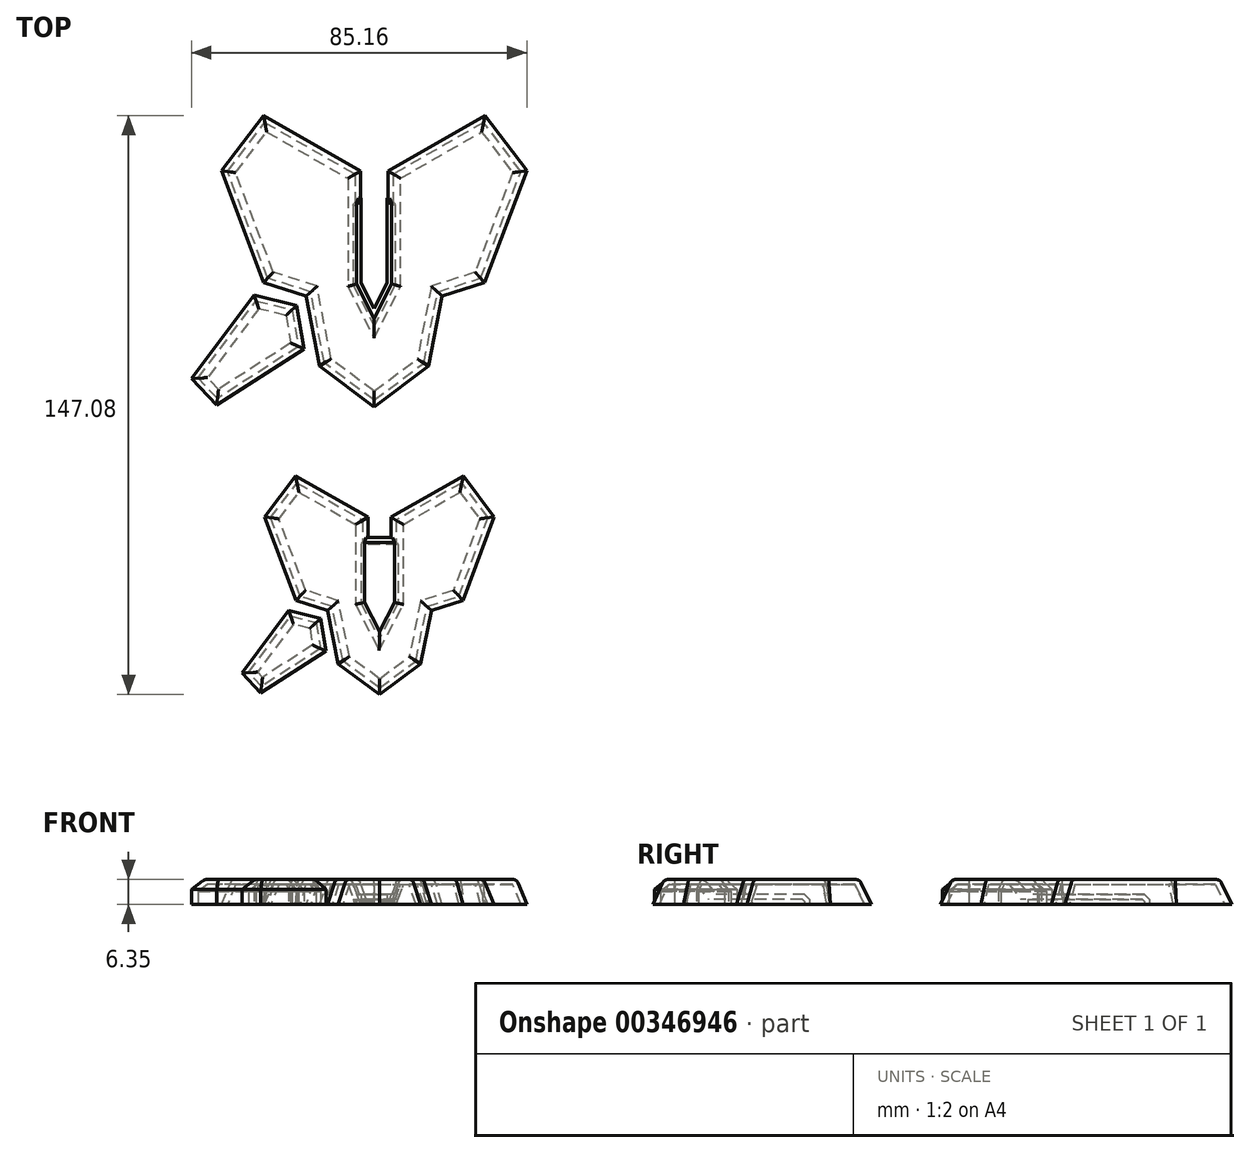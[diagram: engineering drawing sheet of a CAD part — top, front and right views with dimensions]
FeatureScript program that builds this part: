
annotation { "Feature Type Name" : "Feature", "Feature Type Description" : "" }
export const myFeature = defineFeature(function(context is Context, id is Id, definition is map)
    precondition{}
    {
        {
            var Q0;
            Q0=qCreatedBy(makeId("Top.planeOp"),FACE);
            var sketch = newSketch(context, id + "F0", { "sketchPlane" : qUnion([Q0])});
            skLineSegment(sketch, "E0", {"start": v(0.22, 21.79) * mm, "end": v(-3.27, 28.65) * mm});
            skLineSegment(sketch, "E1", {"start": v(-3.27, 28.65) * mm, "end": v(-3.27, 57.26) * mm});
            skLineSegment(sketch, "E2", {"start": v(-3.27, 57.26) * mm, "end": v(-28.23, 71.53) * mm});
            skLineSegment(sketch, "E3", {"start": v(-28.23, 71.53) * mm, "end": v(-39.05, 57.26) * mm});
            skLineSegment(sketch, "E4", {"start": v(-39.05, 57.26) * mm, "end": v(-28.26, 28.65) * mm});
            skLineSegment(sketch, "E5", {"start": v(-28.26, 28.65) * mm, "end": v(-17.5, 25.2) * mm});
            skLineSegment(sketch, "E6", {"start": v(-17.5, 25.2) * mm, "end": v(-14.07, 7.42) * mm});
            skLineSegment(sketch, "E7", {"start": v(-14.07, 7.42) * mm, "end": v(0.22, -3.25) * mm});
            skLineSegment(sketch, "E8", {"start": v(-30.55, 25.57) * mm, "end": v(-19.72, 22.92) * mm});
            skLineSegment(sketch, "E9", {"start": v(-19.72, 22.92) * mm, "end": v(-17.85, 11.94) * mm});
            skLineSegment(sketch, "E10", {"start": v(-17.85, 11.94) * mm, "end": v(-40.04, -2.32) * mm});
            skLineSegment(sketch, "E11", {"start": v(-40.04, -2.32) * mm, "end": v(-46.37, 4.42) * mm});
            skLineSegment(sketch, "E12", {"start": v(-46.37, 4.42) * mm, "end": v(-30.55, 25.57) * mm});
            skLineSegment(sketch, "E13", {"start": v(0.22, 18.03) * mm, "end": v(-6.84, 28.75) * mm});
            skLineSegment(sketch, "E14", {"start": v(-6.84, 28.75) * mm, "end": v(-6.84, 50.27) * mm});
            skLineSegment(sketch, "E15", {"start": v(-6.84, 50.27) * mm, "end": v(0.22, 50.27) * mm});
            skLineSegment(sketch, "E16.MirrorCS", {"start": v(6.84, 50.27) * mm, "end": v(-0.22, 50.27) * mm});
            skLineSegment(sketch, "E17.MirrorCS", {"start": v(6.84, 28.75) * mm, "end": v(6.84, 50.27) * mm});
            skLineSegment(sketch, "E18.MirrorCS", {"start": v(3.27, 28.65) * mm, "end": v(3.27, 57.26) * mm});
            skLineSegment(sketch, "E19.MirrorCS", {"start": v(-0.22, 21.79) * mm, "end": v(3.27, 28.65) * mm});
            skLineSegment(sketch, "E20.MirrorCS", {"start": v(-0.22, 18.03) * mm, "end": v(6.84, 28.75) * mm});
            skLineSegment(sketch, "E21.MirrorCS", {"start": v(3.27, 57.26) * mm, "end": v(28.23, 71.53) * mm});
            skLineSegment(sketch, "E22.MirrorCS", {"start": v(28.23, 71.53) * mm, "end": v(39.05, 57.26) * mm});
            skLineSegment(sketch, "E23.MirrorCS", {"start": v(39.05, 57.26) * mm, "end": v(28.26, 28.65) * mm});
            skLineSegment(sketch, "E24.MirrorCS", {"start": v(28.26, 28.65) * mm, "end": v(17.5, 25.2) * mm});
            skLineSegment(sketch, "E25.MirrorCS", {"start": v(17.5, 25.2) * mm, "end": v(14.07, 7.42) * mm});
            skLineSegment(sketch, "E26.MirrorCS", {"start": v(14.07, 7.42) * mm, "end": v(-0.22, -3.25) * mm});
            skLineSegment(sketch, "E27", {"start": v(1.32, -60) * mm, "end": v(-4.03, -52.16) * mm});
            skLineSegment(sketch, "E28", {"start": v(-4.03, -52.16) * mm, "end": v(-4.03, -36.02) * mm});
            skLineSegment(sketch, "E29", {"start": v(-4.03, -36.02) * mm, "end": v(1.32, -36.02) * mm});
            skLineSegment(sketch, "E30", {"start": v(1.32, -57.3) * mm, "end": v(-1.33, -52.15) * mm});
            skLineSegment(sketch, "E31", {"start": v(-1.33, -52.15) * mm, "end": v(-1.33, -30.7) * mm});
            skLineSegment(sketch, "E32", {"start": v(-1.33, -30.7) * mm, "end": v(-20.04, -20.02) * mm});
            skLineSegment(sketch, "E33", {"start": v(-20.04, -20.02) * mm, "end": v(-28.1, -30.7) * mm});
            skLineSegment(sketch, "E34", {"start": v(-28.1, -30.7) * mm, "end": v(-20.05, -52.16) * mm});
            skLineSegment(sketch, "E35", {"start": v(-20.05, -52.16) * mm, "end": v(-12.05, -54.72) * mm});
            skLineSegment(sketch, "E36", {"start": v(-12.05, -54.72) * mm, "end": v(-9.4, -68.22) * mm});
            skLineSegment(sketch, "E37", {"start": v(-9.4, -68.22) * mm, "end": v(1.32, -76.13) * mm});
            skLineSegment(sketch, "E38", {"start": v(-21.76, -54.5) * mm, "end": v(-13.62, -56.57) * mm});
            skLineSegment(sketch, "E39", {"start": v(-13.62, -56.57) * mm, "end": v(-12.28, -64.82) * mm});
            skLineSegment(sketch, "E40", {"start": v(-12.28, -64.82) * mm, "end": v(-28.87, -75.48) * mm});
            skLineSegment(sketch, "E41", {"start": v(-28.87, -75.48) * mm, "end": v(-33.57, -70.4) * mm});
            skLineSegment(sketch, "E42", {"start": v(-33.57, -70.4) * mm, "end": v(-21.76, -54.5) * mm});
            skLineSegment(sketch, "E43", {"start": v(1.32, -60) * mm, "end": v(6.62, -52.16) * mm});
            skLineSegment(sketch, "E44", {"start": v(6.62, -52.16) * mm, "end": v(6.62, -36.02) * mm});
            skLineSegment(sketch, "E45", {"start": v(6.62, -36.02) * mm, "end": v(1.32, -36.02) * mm});
            skLineSegment(sketch, "E46", {"start": v(1.32, -57.3) * mm, "end": v(4.01, -52.16) * mm});
            skLineSegment(sketch, "E47", {"start": v(4.01, -52.16) * mm, "end": v(4.01, -30.7) * mm});
            skLineSegment(sketch, "E48", {"start": v(4.01, -30.7) * mm, "end": v(22.7, -20.02) * mm});
            skLineSegment(sketch, "E49", {"start": v(22.7, -20.02) * mm, "end": v(30.68, -30.7) * mm});
            skLineSegment(sketch, "E50", {"start": v(30.68, -30.7) * mm, "end": v(22.76, -52.16) * mm});
            skLineSegment(sketch, "E51", {"start": v(22.76, -52.16) * mm, "end": v(14.75, -54.72) * mm});
            skLineSegment(sketch, "E52", {"start": v(14.75, -54.72) * mm, "end": v(12, -68.22) * mm});
            skLineSegment(sketch, "E53", {"start": v(12, -68.22) * mm, "end": v(1.32, -76.13) * mm});
            skSolve(sketch);
        }
        {
            var Q0;
            {var subQ0=sQuery(id+"F0.wireOp",EDGE,"E16.MirrorCS");var subQ1=makeQuery(id+"F0.imprint","IMPRINT",VERTEX,{"derivedFrom":subQ0});Q0=makeQuery(id+"F0.imprint","IMPRINT",FACE,{"disambiguationData":[TD([[makeQuery(id+"F0.imprint","IMPRINT",EDGE,{"disambiguationData":[TD([[subQ1,1.0]])],"derivedFrom":subQ0}),1.0]])]});}
            var Q1;
            {var subQ6=sQuery(id+"F0.wireOp",EDGE,"E30");Q1=makeQuery(id+"F0.imprint","IMPRINT",FACE,{"disambiguationData":[TD([[makeQuery(id+"F0.imprint","IMPRINT",EDGE,{"derivedFrom":subQ6}),-1.0]])]});}
            var Q2;
            {var subQ0=sQuery(id+"F0.wireOp",EDGE,"E14");Q2=makeQuery(id+"F0.imprint","IMPRINT",FACE,{"disambiguationData":[TD([[makeQuery(id+"F0.imprint","IMPRINT",EDGE,{"derivedFrom":subQ0}),-1.0]])]});}
            var Q3;
            Q3=makeQuery(id+"F0.imprint","IMPRINT",FACE,{"disambiguationData":[TD([[makeQuery(id+"F0.imprint","IMPRINT",EDGE,{"derivedFrom":sQuery(id+"F0.wireOp",EDGE,"E27")}),-1.0]])]});
            extrude(context, id + "F1", {"entities" : qUnion([Q0, Q1, Q2, Q3]), "depth" : 2.54 * mm});
        }
        {
            var Q0;
            {var subQ5=sQuery(id+"F0.wireOp",EDGE,"E2");Q0=makeQuery(id+"F0.imprint","IMPRINT",FACE,{"disambiguationData":[TD([[makeQuery(id+"F0.imprint","IMPRINT",EDGE,{"derivedFrom":subQ5}),1.0]])]});}
            var Q1;
            {var subQ0=sQuery(id+"F0.wireOp",EDGE,"E14");Q1=makeQuery(id+"F0.imprint","IMPRINT",FACE,{"disambiguationData":[TD([[makeQuery(id+"F0.imprint","IMPRINT",EDGE,{"derivedFrom":subQ0}),-1.0]])]});}
            var Q2;
            Q2=makeQuery(id+"F0.imprint","IMPRINT",FACE,{"disambiguationData":[TD([[makeQuery(id+"F0.imprint","IMPRINT",EDGE,{"derivedFrom":sQuery(id+"F0.wireOp",EDGE,"E27")}),-1.0]])]});
            var Q3;
            Q3=makeQuery(id+"F0.imprint","IMPRINT",FACE,{"disambiguationData":[TD([[makeQuery(id+"F0.imprint","IMPRINT",EDGE,{"derivedFrom":sQuery(id+"F0.wireOp",EDGE,"E27")}),1.0]])]});
            var Q4;
            Q4=makeQuery(id+"F0.imprint","IMPRINT",FACE,{"disambiguationData":[TD([[makeQuery(id+"F0.imprint","IMPRINT",EDGE,{"derivedFrom":sQuery(id+"F0.wireOp",EDGE,"E8")}),-1.0]])]});
            var Q5;
            Q5=makeQuery(id+"F0.imprint","IMPRINT",FACE,{"disambiguationData":[TD([[makeQuery(id+"F0.imprint","IMPRINT",EDGE,{"derivedFrom":sQuery(id+"F0.wireOp",EDGE,"E38")}),-1.0]])]});
            extrude(context, id + "F2", {"entities" : qUnion([Q0, Q1, Q2, Q3, Q4, Q5]), "depth" : 6.35 * mm});
        }
        {
            var Q0;
            Q0=makeQuery(id+"F2.opExtrude","CAP_FACE",FACE,{"disambiguationData":[OSD([sQuery(id+"F0.wireOp",EDGE,"E0"),sQuery(id+"F0.wireOp",EDGE,"E1"),sQuery(id+"F0.wireOp",EDGE,"E2"),sQuery(id+"F0.wireOp",EDGE,"E3"),sQuery(id+"F0.wireOp",EDGE,"E4"),sQuery(id+"F0.wireOp",EDGE,"E5"),sQuery(id+"F0.wireOp",EDGE,"E6"),sQuery(id+"F0.wireOp",EDGE,"E7"),sQuery(id+"F0.wireOp",EDGE,"E18.MirrorCS"),sQuery(id+"F0.wireOp",EDGE,"E19.MirrorCS"),sQuery(id+"F0.wireOp",EDGE,"E21.MirrorCS"),sQuery(id+"F0.wireOp",EDGE,"E22.MirrorCS"),sQuery(id+"F0.wireOp",EDGE,"E23.MirrorCS"),sQuery(id+"F0.wireOp",EDGE,"E24.MirrorCS"),sQuery(id+"F0.wireOp",EDGE,"E25.MirrorCS"),sQuery(id+"F0.wireOp",EDGE,"E26.MirrorCS")])],"isStart":false});
            var Q1;
            Q1=makeQuery(id+"F2.opExtrude","CAP_FACE",FACE,{"disambiguationData":[OSD([sQuery(id+"F0.wireOp",EDGE,"E30"),sQuery(id+"F0.wireOp",EDGE,"E31"),sQuery(id+"F0.wireOp",EDGE,"E32"),sQuery(id+"F0.wireOp",EDGE,"E33"),sQuery(id+"F0.wireOp",EDGE,"E34"),sQuery(id+"F0.wireOp",EDGE,"E35"),sQuery(id+"F0.wireOp",EDGE,"E36"),sQuery(id+"F0.wireOp",EDGE,"E37"),sQuery(id+"F0.wireOp",EDGE,"E46"),sQuery(id+"F0.wireOp",EDGE,"E47"),sQuery(id+"F0.wireOp",EDGE,"E48"),sQuery(id+"F0.wireOp",EDGE,"E49"),sQuery(id+"F0.wireOp",EDGE,"E50"),sQuery(id+"F0.wireOp",EDGE,"E51"),sQuery(id+"F0.wireOp",EDGE,"E52"),sQuery(id+"F0.wireOp",EDGE,"E53")])],"isStart":false});
            chamfer(context, id + "F3", {"entities" : qUnion([Q0, Q1]), "chamferType" : ChamferType.OFFSET_ANGLE, "width" : 2.54 * mm, "oppositeDirection" : false, "angle" : 70 * degree, "tangentPropagation" : true});
        }
        {
            var Q0;
            Q0=makeQuery(id+"F1.opExtrude","CAP_EDGE",EDGE,{"disambiguationData":[OSD([sQuery(id+"F0.wireOp",EDGE,"E15"),sQuery(id+"F0.wireOp",EDGE,"E16.MirrorCS")])],"isStart":false});
            var Q1;
            Q1=makeQuery(id+"F1.opExtrude","CAP_EDGE",EDGE,{"disambiguationData":[OSD([sQuery(id+"F0.wireOp",EDGE,"E29"),sQuery(id+"F0.wireOp",EDGE,"E45")])],"isStart":false});
            chamfer(context, id + "F4", {"entities" : qUnion([Q0, Q1]), "width" : 1.27 * mm, "tangentPropagation" : true});
        }
        {
            var Q0;
            Q0=makeQuery(id+"F2.opExtrude","CAP_FACE",FACE,{"disambiguationData":[OSD([sQuery(id+"F0.wireOp",EDGE,"E0"),sQuery(id+"F0.wireOp",EDGE,"E1"),sQuery(id+"F0.wireOp",EDGE,"E2"),sQuery(id+"F0.wireOp",EDGE,"E3"),sQuery(id+"F0.wireOp",EDGE,"E4"),sQuery(id+"F0.wireOp",EDGE,"E5"),sQuery(id+"F0.wireOp",EDGE,"E6"),sQuery(id+"F0.wireOp",EDGE,"E7"),sQuery(id+"F0.wireOp",EDGE,"E18.MirrorCS"),sQuery(id+"F0.wireOp",EDGE,"E19.MirrorCS"),sQuery(id+"F0.wireOp",EDGE,"E21.MirrorCS"),sQuery(id+"F0.wireOp",EDGE,"E22.MirrorCS"),sQuery(id+"F0.wireOp",EDGE,"E23.MirrorCS"),sQuery(id+"F0.wireOp",EDGE,"E24.MirrorCS"),sQuery(id+"F0.wireOp",EDGE,"E25.MirrorCS"),sQuery(id+"F0.wireOp",EDGE,"E26.MirrorCS")])],"isStart":false});
            var Q1;
            Q1=makeQuery(id+"F2.opExtrude","CAP_FACE",FACE,{"disambiguationData":[OSD([sQuery(id+"F0.wireOp",EDGE,"E30"),sQuery(id+"F0.wireOp",EDGE,"E31"),sQuery(id+"F0.wireOp",EDGE,"E32"),sQuery(id+"F0.wireOp",EDGE,"E33"),sQuery(id+"F0.wireOp",EDGE,"E34"),sQuery(id+"F0.wireOp",EDGE,"E35"),sQuery(id+"F0.wireOp",EDGE,"E36"),sQuery(id+"F0.wireOp",EDGE,"E37"),sQuery(id+"F0.wireOp",EDGE,"E46"),sQuery(id+"F0.wireOp",EDGE,"E47"),sQuery(id+"F0.wireOp",EDGE,"E48"),sQuery(id+"F0.wireOp",EDGE,"E49"),sQuery(id+"F0.wireOp",EDGE,"E50"),sQuery(id+"F0.wireOp",EDGE,"E51"),sQuery(id+"F0.wireOp",EDGE,"E52"),sQuery(id+"F0.wireOp",EDGE,"E53")])],"isStart":false});
            fillet(context, id + "F5", {"entities" : qUnion([Q0, Q1]), "radius" : 1.27 * mm, "tangentPropagation" : true, "allowEdgeOverflow" : false});
        }
        {
            var Q0;
            Q0=makeQuery(id+"F2.opExtrude","CAP_FACE",FACE,{"disambiguationData":[OSD([sQuery(id+"F0.wireOp",EDGE,"E8"),sQuery(id+"F0.wireOp",EDGE,"E9"),sQuery(id+"F0.wireOp",EDGE,"E10"),sQuery(id+"F0.wireOp",EDGE,"E11"),sQuery(id+"F0.wireOp",EDGE,"E12")])],"isStart":false});
            var Q1;
            Q1=makeQuery(id+"F2.opExtrude","CAP_FACE",FACE,{"disambiguationData":[OSD([sQuery(id+"F0.wireOp",EDGE,"E38"),sQuery(id+"F0.wireOp",EDGE,"E39"),sQuery(id+"F0.wireOp",EDGE,"E40"),sQuery(id+"F0.wireOp",EDGE,"E41"),sQuery(id+"F0.wireOp",EDGE,"E42")])],"isStart":false});
            chamfer(context, id + "F6", {"entities" : qUnion([Q0, Q1]), "width" : 2.54 * mm, "tangentPropagation" : true});
        }
        {
            var Q0;
            Q0=makeQuery(id+"F2.opExtrude","CAP_FACE",FACE,{"disambiguationData":[OSD([sQuery(id+"F0.wireOp",EDGE,"E8"),sQuery(id+"F0.wireOp",EDGE,"E9"),sQuery(id+"F0.wireOp",EDGE,"E10"),sQuery(id+"F0.wireOp",EDGE,"E11"),sQuery(id+"F0.wireOp",EDGE,"E12")])],"isStart":false});
            var Q1;
            Q1=makeQuery(id+"F2.opExtrude","CAP_FACE",FACE,{"disambiguationData":[OSD([sQuery(id+"F0.wireOp",EDGE,"E38"),sQuery(id+"F0.wireOp",EDGE,"E39"),sQuery(id+"F0.wireOp",EDGE,"E40"),sQuery(id+"F0.wireOp",EDGE,"E41"),sQuery(id+"F0.wireOp",EDGE,"E42")])],"isStart":false});
            fillet(context, id + "F7", {"entities" : qUnion([Q0, Q1]), "radius" : 1.27 * mm, "tangentPropagation" : true, "allowEdgeOverflow" : false});
        }
        {
            var Q0;
            Q0=makeQuery(id+"F2.opExtrude","SWEPT_BODY",BODY,{"disambiguationData":[OSD([sQuery(id+"F0.wireOp",EDGE,"E30"),sQuery(id+"F0.wireOp",EDGE,"E31"),sQuery(id+"F0.wireOp",EDGE,"E32"),sQuery(id+"F0.wireOp",EDGE,"E33"),sQuery(id+"F0.wireOp",EDGE,"E34"),sQuery(id+"F0.wireOp",EDGE,"E35"),sQuery(id+"F0.wireOp",EDGE,"E36"),sQuery(id+"F0.wireOp",EDGE,"E37"),sQuery(id+"F0.wireOp",EDGE,"E46"),sQuery(id+"F0.wireOp",EDGE,"E47"),sQuery(id+"F0.wireOp",EDGE,"E48"),sQuery(id+"F0.wireOp",EDGE,"E49"),sQuery(id+"F0.wireOp",EDGE,"E50"),sQuery(id+"F0.wireOp",EDGE,"E51"),sQuery(id+"F0.wireOp",EDGE,"E52"),sQuery(id+"F0.wireOp",EDGE,"E53")])]});
            var Q1;
            Q1=makeQuery(id+"F1.opExtrude","SWEPT_BODY",BODY,{"disambiguationData":[OSD([sQuery(id+"F0.wireOp",EDGE,"E27"),sQuery(id+"F0.wireOp",EDGE,"E28"),sQuery(id+"F0.wireOp",EDGE,"E29"),sQuery(id+"F0.wireOp",EDGE,"E43"),sQuery(id+"F0.wireOp",EDGE,"E44"),sQuery(id+"F0.wireOp",EDGE,"E45")])]});
            booleanBodies(context, id + "F8", {"operationType" : BooleanOperationType.UNION, "tools" : qUnion([Q0, Q1])});
        }
        {
            var Q0;
            Q0=makeQuery(id+"F2.opExtrude","SWEPT_BODY",BODY,{"disambiguationData":[OSD([sQuery(id+"F0.wireOp",EDGE,"E0"),sQuery(id+"F0.wireOp",EDGE,"E1"),sQuery(id+"F0.wireOp",EDGE,"E2"),sQuery(id+"F0.wireOp",EDGE,"E3"),sQuery(id+"F0.wireOp",EDGE,"E4"),sQuery(id+"F0.wireOp",EDGE,"E5"),sQuery(id+"F0.wireOp",EDGE,"E6"),sQuery(id+"F0.wireOp",EDGE,"E7"),sQuery(id+"F0.wireOp",EDGE,"E18.MirrorCS"),sQuery(id+"F0.wireOp",EDGE,"E19.MirrorCS"),sQuery(id+"F0.wireOp",EDGE,"E21.MirrorCS"),sQuery(id+"F0.wireOp",EDGE,"E22.MirrorCS"),sQuery(id+"F0.wireOp",EDGE,"E23.MirrorCS"),sQuery(id+"F0.wireOp",EDGE,"E24.MirrorCS"),sQuery(id+"F0.wireOp",EDGE,"E25.MirrorCS"),sQuery(id+"F0.wireOp",EDGE,"E26.MirrorCS")])]});
            var Q1;
            Q1=makeQuery(id+"F1.opExtrude","SWEPT_BODY",BODY,{"disambiguationData":[OSD([sQuery(id+"F0.wireOp",EDGE,"E13"),sQuery(id+"F0.wireOp",EDGE,"E14"),sQuery(id+"F0.wireOp",EDGE,"E15"),sQuery(id+"F0.wireOp",EDGE,"E16.MirrorCS"),sQuery(id+"F0.wireOp",EDGE,"E17.MirrorCS"),sQuery(id+"F0.wireOp",EDGE,"E20.MirrorCS")])]});
            booleanBodies(context, id + "F9", {"operationType" : BooleanOperationType.UNION, "tools" : qUnion([Q0, Q1])});
        }
        {
            var Q0;
            Q0=makeQuery(id+"F8.opBoolean","MERGE",FACE,{"derivedFrom":[makeQuery(id+"F1.opExtrude","CAP_FACE",FACE,{"disambiguationData":[OSD([sQuery(id+"F0.wireOp",EDGE,"E27"),sQuery(id+"F0.wireOp",EDGE,"E28"),sQuery(id+"F0.wireOp",EDGE,"E29"),sQuery(id+"F0.wireOp",EDGE,"E43"),sQuery(id+"F0.wireOp",EDGE,"E44"),sQuery(id+"F0.wireOp",EDGE,"E45")])],"isStart":true}),makeQuery(id+"F2.opExtrude","CAP_FACE",FACE,{"disambiguationData":[OSD([sQuery(id+"F0.wireOp",EDGE,"E30"),sQuery(id+"F0.wireOp",EDGE,"E31"),sQuery(id+"F0.wireOp",EDGE,"E32"),sQuery(id+"F0.wireOp",EDGE,"E33"),sQuery(id+"F0.wireOp",EDGE,"E34"),sQuery(id+"F0.wireOp",EDGE,"E35"),sQuery(id+"F0.wireOp",EDGE,"E36"),sQuery(id+"F0.wireOp",EDGE,"E37"),sQuery(id+"F0.wireOp",EDGE,"E46"),sQuery(id+"F0.wireOp",EDGE,"E47"),sQuery(id+"F0.wireOp",EDGE,"E48"),sQuery(id+"F0.wireOp",EDGE,"E49"),sQuery(id+"F0.wireOp",EDGE,"E50"),sQuery(id+"F0.wireOp",EDGE,"E51"),sQuery(id+"F0.wireOp",EDGE,"E52"),sQuery(id+"F0.wireOp",EDGE,"E53")])],"isStart":true})]});
            shell(context, id + "F10", {"entities" : qUnion([Q0]), "thickness" : 1.27 * mm});
        }
        {
            var Q0;
            Q0=makeQuery(id+"F9.opBoolean","MERGE",FACE,{"derivedFrom":[makeQuery(id+"F1.opExtrude","CAP_FACE",FACE,{"disambiguationData":[OSD([sQuery(id+"F0.wireOp",EDGE,"E13"),sQuery(id+"F0.wireOp",EDGE,"E14"),sQuery(id+"F0.wireOp",EDGE,"E15"),sQuery(id+"F0.wireOp",EDGE,"E16.MirrorCS"),sQuery(id+"F0.wireOp",EDGE,"E17.MirrorCS"),sQuery(id+"F0.wireOp",EDGE,"E20.MirrorCS")])],"isStart":true}),makeQuery(id+"F2.opExtrude","CAP_FACE",FACE,{"disambiguationData":[OSD([sQuery(id+"F0.wireOp",EDGE,"E0"),sQuery(id+"F0.wireOp",EDGE,"E1"),sQuery(id+"F0.wireOp",EDGE,"E2"),sQuery(id+"F0.wireOp",EDGE,"E3"),sQuery(id+"F0.wireOp",EDGE,"E4"),sQuery(id+"F0.wireOp",EDGE,"E5"),sQuery(id+"F0.wireOp",EDGE,"E6"),sQuery(id+"F0.wireOp",EDGE,"E7"),sQuery(id+"F0.wireOp",EDGE,"E18.MirrorCS"),sQuery(id+"F0.wireOp",EDGE,"E19.MirrorCS"),sQuery(id+"F0.wireOp",EDGE,"E21.MirrorCS"),sQuery(id+"F0.wireOp",EDGE,"E22.MirrorCS"),sQuery(id+"F0.wireOp",EDGE,"E23.MirrorCS"),sQuery(id+"F0.wireOp",EDGE,"E24.MirrorCS"),sQuery(id+"F0.wireOp",EDGE,"E25.MirrorCS"),sQuery(id+"F0.wireOp",EDGE,"E26.MirrorCS")])],"isStart":true})]});
            shell(context, id + "F11", {"entities" : qUnion([Q0]), "thickness" : 1.27 * mm});
        }
        {
            var Q0;
            Q0=makeQuery(id+"F2.opExtrude","CAP_FACE",FACE,{"disambiguationData":[OSD([sQuery(id+"F0.wireOp",EDGE,"E38"),sQuery(id+"F0.wireOp",EDGE,"E39"),sQuery(id+"F0.wireOp",EDGE,"E40"),sQuery(id+"F0.wireOp",EDGE,"E41"),sQuery(id+"F0.wireOp",EDGE,"E42")])],"isStart":true});
            shell(context, id + "F12", {"entities" : qUnion([Q0]), "thickness" : 1.27 * mm});
        }
        {
            var Q0;
            Q0=makeQuery(id+"F2.opExtrude","CAP_FACE",FACE,{"disambiguationData":[OSD([sQuery(id+"F0.wireOp",EDGE,"E8"),sQuery(id+"F0.wireOp",EDGE,"E9"),sQuery(id+"F0.wireOp",EDGE,"E10"),sQuery(id+"F0.wireOp",EDGE,"E11"),sQuery(id+"F0.wireOp",EDGE,"E12")])],"isStart":true});
            shell(context, id + "F13", {"entities" : qUnion([Q0]), "thickness" : 1.27 * mm});
        }
    });
